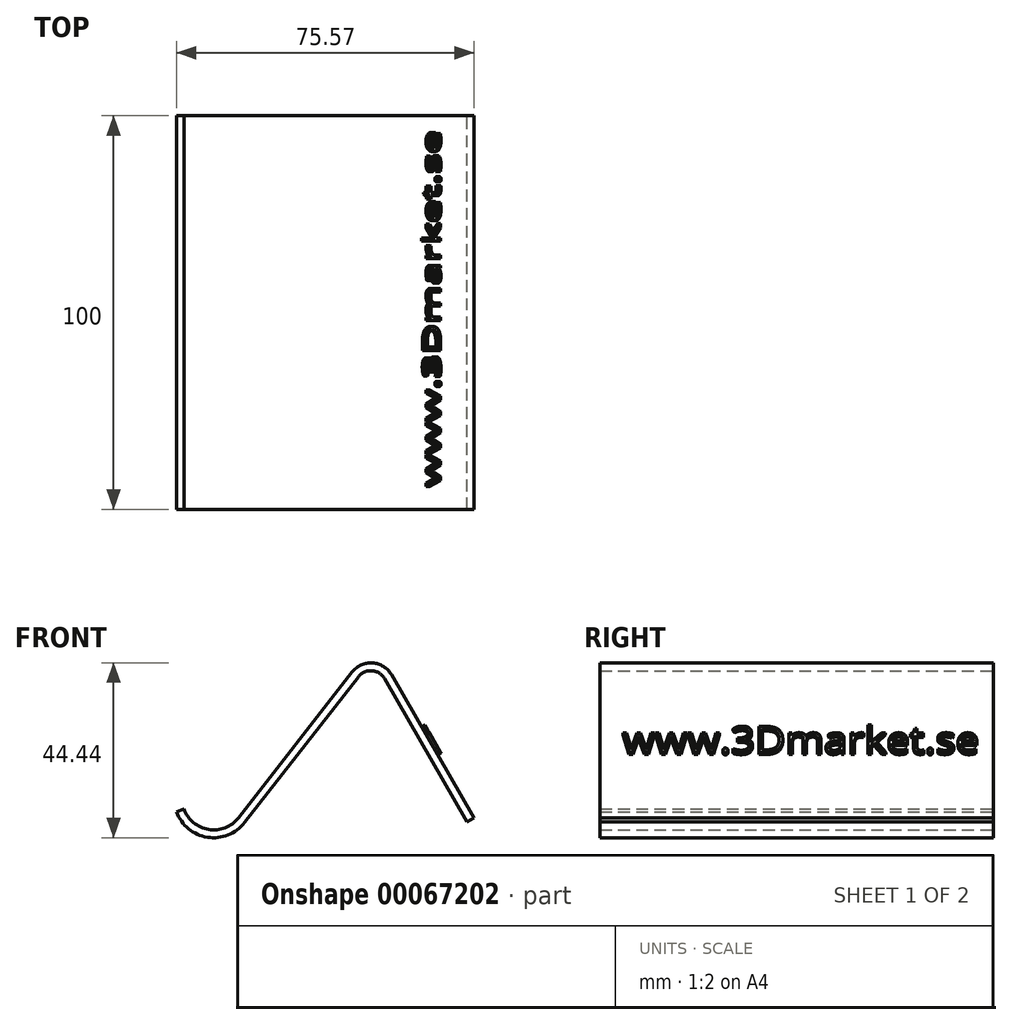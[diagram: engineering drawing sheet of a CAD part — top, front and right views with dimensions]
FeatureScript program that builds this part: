
annotation { "Feature Type Name" : "Feature", "Feature Type Description" : "" }
export const myFeature = defineFeature(function(context is Context, id is Id, definition is map)
    precondition{}
    {
        {
            var Q0;
            Q0=qCreatedBy(makeId("Front.planeOp"),FACE);
            var sketch = newSketch(context, id + "F0", { "sketchPlane" : qUnion([Q0])});
            skLineSegment(sketch, "E0", {"start": v(25.47, 0) * mm, "end": v(4.45, 36.36) * mm});
            skLineSegment(sketch, "E1", {"start": v(-5.47, 37.05) * mm, "end": v(-34.4, 0) * mm});
            skPoint(sketch, "E2.visualSharp", {"position": v(0, 44.06) * mm});
            skArc(sketch, "E2.filletArc", {"start": v(4.45, 36.36) * mm, "mid": v(-0.33, 39.35) * mm, "end": v(-5.47, 37.05) * mm});
            skArc(sketch, "E3", {"start": v(-48.22, 2.2) * mm, "mid": v(-41.95, -2.98) * mm, "end": v(-34.4, 0) * mm});
            skLineSegment(sketch, "E4.0", {"start": v(23.74, -1) * mm, "end": v(2.72, 35.36) * mm});
            skArc(sketch, "E4.1", {"start": v(2.72, 35.36) * mm, "mid": v(-0.47, 37.35) * mm, "end": v(-3.9, 35.82) * mm});
            skLineSegment(sketch, "E4.2", {"start": v(-3.9, 35.82) * mm, "end": v(-32.81, -1.23) * mm});
            skArc(sketch, "E4.3", {"start": v(-50.1, 1.51) * mm, "mid": v(-42.26, -4.95) * mm, "end": v(-32.81, -1.23) * mm});
            skLineSegment(sketch, "E5", {"start": v(-50.1, 1.51) * mm, "end": v(-48.22, 2.2) * mm});
            skLineSegment(sketch, "E6", {"start": v(23.74, -1) * mm, "end": v(25.47, 0) * mm});
            skSolve(sketch);
        }
        {
            var Q0;
            Q0=makeQuery(id+"F0.imprint","IMPRINT",FACE,{"disambiguationData":[TD([[makeQuery(id+"F0.imprint","IMPRINT",EDGE,{"derivedFrom":sQuery(id+"F0.wireOp",EDGE,"E0")}),1.0]])]});
            extrude(context, id + "F1", {"entities" : qUnion([Q0]), "depth" : 100 * mm});
        }
        {
            var Q0;
            Q0=makeQuery(id+"F1.opExtrude","SWEPT_FACE",FACE,{"disambiguationData":[OSD([sQuery(id+"F0.wireOp",EDGE,"E0")])]});
            var sketch = newSketch(context, id + "F2", { "sketchPlane" : qUnion([Q0])});
            skText(sketch, "E7", { "text": "www.3Dmarket.se", "fontName": "OpenSans-Regular.ttf"});
            const initialGuessF2  = {"E7": [-0.0943, 0.00587, 1, 0, 0.00764]};
            skSetInitialGuess(sketch, initialGuessF2);
            skSolve(sketch);
        }
        {
            var Q0;
            Q0 = qSketchRegion(id + "F2", true);
            extrude(context, id + "F3", {"entities" : qUnion([Q0]), "operationType" : NewBodyOperationType.ADD, "depth" : 1 * mm});
        }
    });
